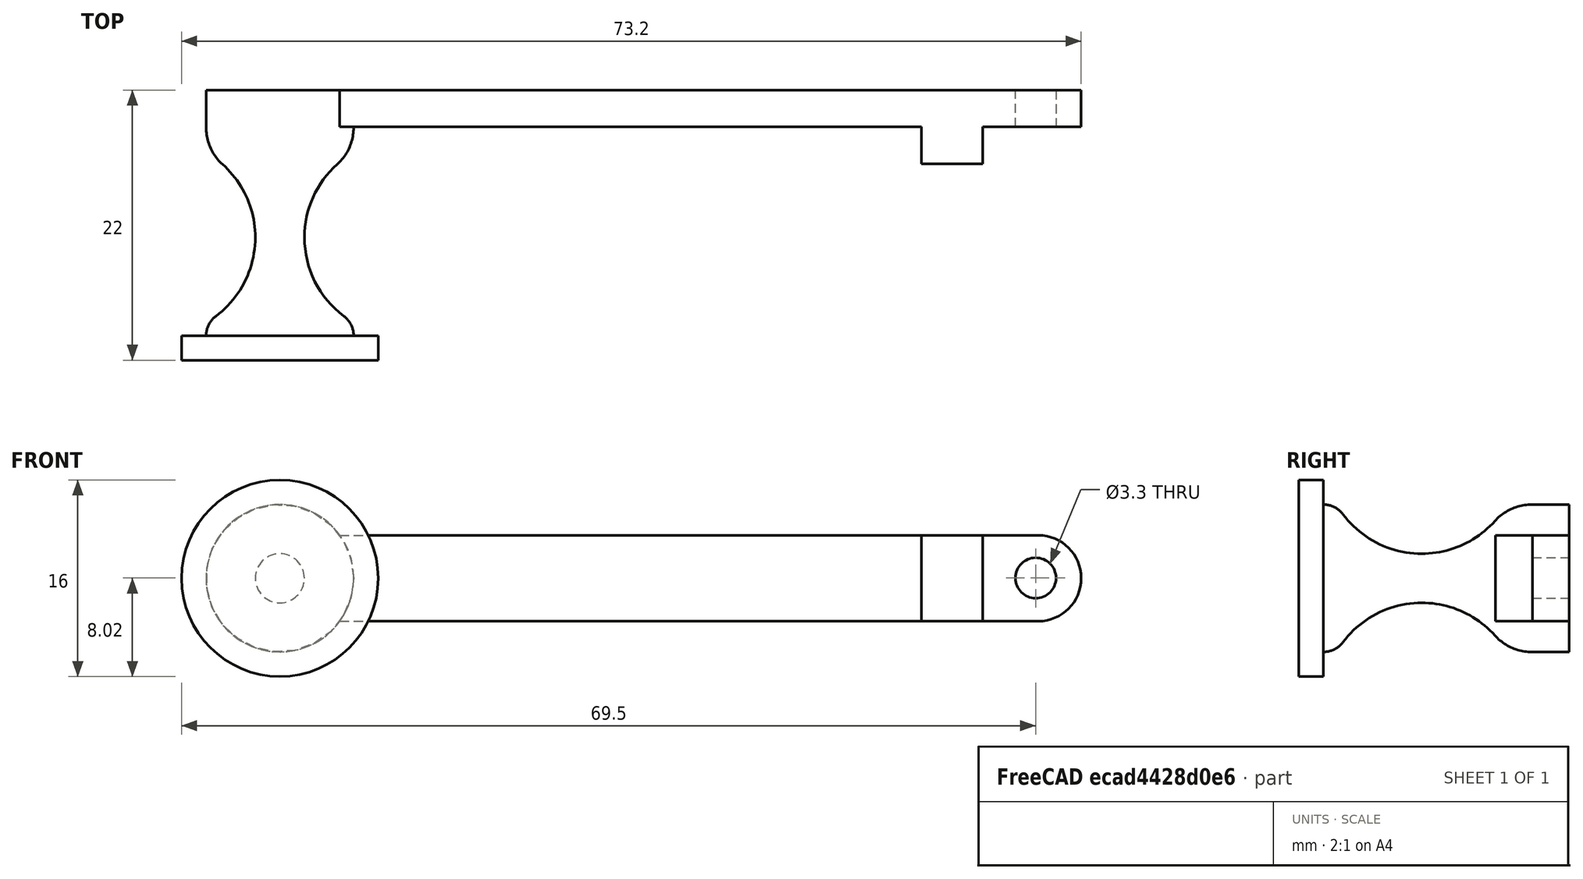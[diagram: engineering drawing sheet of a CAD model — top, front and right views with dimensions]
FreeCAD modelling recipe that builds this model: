
FCSTD DOCUMENT  (FreeCAD 1.0R39109 (Git))
Label: phone holder
License: All rights reserved
LicenseURL: http://en.wikipedia.org/wiki/All_rights_reserved
objects: PartDesign::Fillet×3, PartDesign::AdditiveBox×2, PartDesign::AdditiveCylinder×2, Mesh::Feature×2, PartDesign::SubtractiveCylinder×1, PartDesign::SubtractiveTorus×1, PartDesign::Body×1
note: 28 computed .brp shape members not serialized (recipe doc carries the construction recipe); baked Part::Feature solids carry a one-line shape summary decoded from their .brp

FEATURE [PartDesign::AdditiveBox] Box
  AttacherType = Attacher::AttachEngine3D
  AttachmentSupport = -> [XY_Plane]
  Height = 7
  Length = 70
  MapMode = 5
  Suppressed = false
  Width = 3
FEATURE [PartDesign::Fillet] Fillet
  Base = -> Box [Edge8,Edge6]
  BaseFeature = -> Box
  Radius = 3.49
  SupportTransform = false
  Suppressed = false
  UseAllEdges = false
FEATURE [PartDesign::SubtractiveCylinder] Cylinder
  Angle = 360
  AttacherType = Attacher::AttachEngine3D
  AttachmentOffset = pos=(66.3,3.52,-4) rot=(0,0,1;0rad)
  AttachmentSupport = -> [XZ_Plane]
  BaseFeature = -> Fillet
  FirstAngle = 0
  Height = 5
  MapMode = 5
  Placement = pos=(66.3,4,3.52) rot=(1,0,0;1.5708rad)
  Radius = 1.65
  SecondAngle = 0
  Suppressed = false
FEATURE [PartDesign::AdditiveBox] Box001
  AttacherType = Attacher::AttachEngine3D
  AttachmentOffset = pos=(57,0,0) rot=(0,0,1;0rad)
  AttachmentSupport = -> [XZ_Plane]
  BaseFeature = -> Cylinder
  Height = 3
  Length = 5
  MapMode = 5
  Placement = pos=(57,0,0) rot=(1,0,0;1.5708rad)
  Suppressed = false
  Width = 7
FEATURE [PartDesign::AdditiveCylinder] Cylinder001
  Angle = 360
  AttacherType = Attacher::AttachEngine3D
  AttachmentOffset = pos=(4.8,3.5,-3) rot=(0,0,1;0rad)
  AttachmentSupport = -> [XZ_Plane]
  BaseFeature = -> Box001
  FirstAngle = 0
  Height = 22
  MapMode = 5
  Placement = pos=(4.8,3,3.5) rot=(1,0,0;1.5708rad)
  Radius = 6
  SecondAngle = 0
  Suppressed = false
FEATURE [PartDesign::SubtractiveTorus] Torus
  Angle1 = -180
  Angle2 = 180
  Angle3 = 360
  AttacherType = Attacher::AttachEngine3D
  AttachmentOffset = pos=(4.8,3.5,9) rot=(0,0,1;0rad)
  AttachmentSupport = -> [XZ_Plane]
  BaseFeature = -> Cylinder001
  MapMode = 5
  Placement = pos=(4.8,-9,3.5) rot=(1,0,0;1.5708rad)
  Radius1 = 10
  Radius2 = 8
  Suppressed = false
FEATURE [PartDesign::Fillet] Fillet004
  Base = -> Torus [Edge40]
  BaseFeature = -> Torus
  Placement = pos=(4.8,-9,3.5) rot=(1,0,0;1.5708rad)
  Radius = 4
  SupportTransform = false
  Suppressed = false
  UseAllEdges = false
FEATURE [PartDesign::AdditiveCylinder] Cylinder002
  Angle = 360
  AttacherType = Attacher::AttachEngine3D
  AttachmentOffset = pos=(4.8,3.5,17) rot=(0,0,1;0rad)
  AttachmentSupport = -> [XZ_Plane]
  BaseFeature = -> Fillet004
  FirstAngle = 0
  Height = 2
  MapMode = 5
  Placement = pos=(4.8,-17,3.5) rot=(1,0,0;1.5708rad)
  Radius = 8
  SecondAngle = 0
  Suppressed = false
FEATURE [PartDesign::Fillet] Fillet005
  Base = -> Cylinder002 [Edge47]
  BaseFeature = -> Cylinder002
  Placement = pos=(4.8,-17,3.5) rot=(1,0,0;1.5708rad)
  Radius = 1.99
  SupportTransform = false
  Suppressed = false
  UseAllEdges = false
FEATURE [PartDesign::Body] Body  label="Arm"
  AllowCompound = false
  Group = -> [Box,Fillet,Cylinder,Box001,Cylinder001,Torus,Fillet004,Cylinder002,Fillet005]
  Origin = -> Origin
  Tip = -> Fillet005
FEATURE [Mesh::Feature] Bolt_Short  label="Bolt Short"
  Placement = pos=(13.25,0,0) rot=(0,0,1;0rad)
FEATURE [Mesh::Feature] BoltLong  label="Bolt Long"
